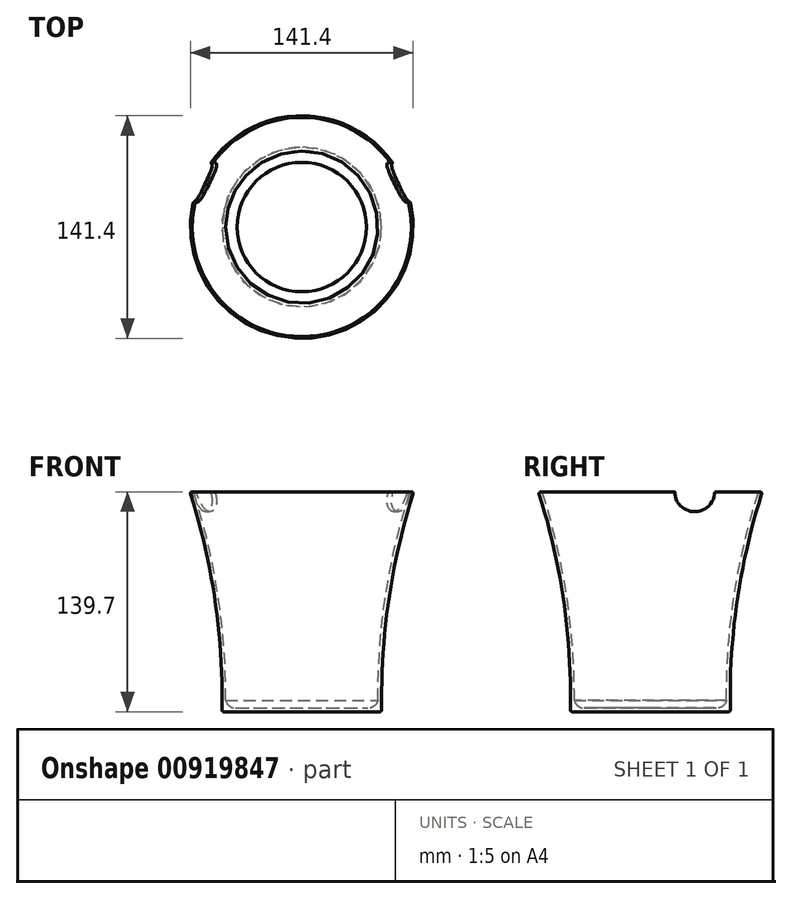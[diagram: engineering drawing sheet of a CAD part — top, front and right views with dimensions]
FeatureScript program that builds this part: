
annotation { "Feature Type Name" : "Feature", "Feature Type Description" : "" }
export const myFeature = defineFeature(function(context is Context, id is Id, definition is map)
    precondition{}
    {
        {
            var Q0;
            Q0=qCreatedBy(makeId("Front.planeOp"),FACE);
            var sketch = newSketch(context, id + "F0", { "sketchPlane" : qUnion([Q0])});
            skLineSegment(sketch, "E0", {"start": v(0, -79.42) * mm, "end": v(50.8, -79.42) * mm});
            skArc(sketch, "E1", {"start": v(76.2, 75.16) * mm, "mid": v(56.34, -0.95) * mm, "end": v(50.8, -79.42) * mm});
            skLineSegment(sketch, "E2", {"start": v(76.2, 75.16) * mm, "end": v(73.82, 75.16) * mm});
            skArc(sketch, "E3", {"start": v(73.82, 75.16) * mm, "mid": v(54.6, 2.68) * mm, "end": v(48.37, -72.04) * mm});
            skLineSegment(sketch, "E4", {"start": v(0, -79.42) * mm, "end": v(0, -77.03) * mm});
            skLineSegment(sketch, "E5", {"start": v(0, -77.03) * mm, "end": v(41.11, -77.03) * mm});
            skArc(sketch, "E6", {"start": v(41.11, -77.03) * mm, "mid": v(45.72, -75.96) * mm, "end": v(48.37, -72.04) * mm});
            skPoint(sketch, "E7", {"position": v(0, -5.65) * mm});
            skLineSegment(sketch, "E8", {"start": v(0, -79.42) * mm, "end": v(0, 60.28) * mm, "construction": true});
            skLineSegment(sketch, "E9", {"start": v(0, 60.28) * mm, "end": v(71.12, 60.28) * mm});
            skSolve(sketch);
        }
        {
            var Q0;
            Q0=makeQuery(id+"F0.imprint","IMPRINT",FACE,{"disambiguationData":[TD([[makeQuery(id+"F0.imprint","IMPRINT",EDGE,{"derivedFrom":sQuery(id+"F0.wireOp",EDGE,"E0")}),1.0]])]});
            var sketch = newSketch(context, id + "F1", { "sketchPlane" : qUnion([Q0])});
            skPoint(sketch, "E10.start.orphan", {"position": v(0, -76.16) * mm});
            skSolve(sketch);
        }
        {
            var Q0;
            Q0=makeQuery(id+"F1.imprint","IMPRINT",FACE,{"disambiguationData":[TD([[makeQuery(id+"F1.imprint","IMPRINT",EDGE,{"derivedFrom":makeQuery(id+"F0.imprint","IMPRINT",EDGE,{"derivedFrom":sQuery(id+"F0.wireOp",EDGE,"E0")})}),1.0]])]});
            var Q1;
            Q1=sQuery(id+"F0.wireOp",EDGE,"E4");
            revolve(context, id + "F2", {"surfaceOperationType" : NewSurfaceOperationType.NEW, "entities" : qUnion([Q0]), "axis" : qUnion([Q1]), "revolveType" : RevolveType.FULL});
        }
        {
            var Q0;
            Q0=qCreatedBy(makeId("Right.planeOp"),FACE);
            var sketch = newSketch(context, id + "F3", { "sketchPlane" : qUnion([Q0])});
            skLineSegment(sketch, "E11", {"start": v(28.17, 63.54) * mm, "end": v(40.87, 63.54) * mm});
            skLineSegment(sketch, "E12", {"start": v(28.17, 63.54) * mm, "end": v(15.47, 63.54) * mm});
            skLineSegment(sketch, "E13", {"start": v(15.47, 63.54) * mm, "end": v(15.47, 60.36) * mm});
            skLineSegment(sketch, "E14", {"start": v(40.87, 63.54) * mm, "end": v(40.87, 60.36) * mm});
            skPoint(sketch, "E15", {"position": v(84.53, 63.54) * mm});
            skArc(sketch, "E16", {"start": v(15.47, 60.36) * mm, "mid": v(28.17, 47.66) * mm, "end": v(40.87, 60.36) * mm});
            skSolve(sketch);
        }
        {
            var Q0;
            Q0=makeQuery(id+"F3.imprint","IMPRINT",FACE,{"disambiguationData":[TD([[makeQuery(id+"F3.imprint","IMPRINT",EDGE,{"derivedFrom":sQuery(id+"F3.wireOp",EDGE,"E11")}),-1.0]])]});
            extrude(context, id + "F4", {"entities" : qUnion([Q0]), "operationType" : NewBodyOperationType.REMOVE, "endBound" : BoundingType.SYMMETRIC, "depth" : 177.8 * mm, "offsetDistance" : 25.4 * mm});
        }
        {
            var Q0;
            Q0=makeQuery(id+"F2.opRevolve","SWEPT_EDGE",EDGE,{"disambiguationData":[OSD([sQuery(id+"F0.wireOp",EDGE,"E0"),sQuery(id+"F0.wireOp",EDGE,"E1")])]});
            fillet(context, id + "F5", {"entities" : qUnion([Q0]), "radius" : 1.27 * mm, "tangentPropagation" : true, "allowEdgeOverflow" : false});
        }
        {
            var Q0;
            {var subQ0=sQuery(id+"F1.wireOp",EDGE,"ap5BJ3xG-dSlw-eity-C2BJ-NnthXKLn69fI");var subQ1=sQuery(id+"F0.wireOp",EDGE,"E1");Q0=makeQuery(id+"F4.boolean.opBoolean","SPLIT",EDGE,{"disambiguationData":[TD([makeQuery(id+"F4.opExtrude","SWEPT_FACE",FACE,{"disambiguationData":[OSD([sQuery(id+"F3.wireOp",EDGE,"E14")])]})])],"derivedFrom":makeQuery(id+"F2.opRevolve","SWEPT_EDGE",EDGE,{"disambiguationData":[OSD([subQ1,subQ0])]})});}
            var Q1;
            {var subQ0=sQuery(id+"F1.wireOp",EDGE,"ap5BJ3xG-dSlw-eity-C2BJ-NnthXKLn69fI");var subQ1=sQuery(id+"F0.wireOp",EDGE,"E3");Q1=makeQuery(id+"F4.boolean.opBoolean","SPLIT",EDGE,{"disambiguationData":[TD([makeQuery(id+"F4.opExtrude","SWEPT_FACE",FACE,{"disambiguationData":[OSD([sQuery(id+"F3.wireOp",EDGE,"E14")])]})])],"derivedFrom":makeQuery(id+"F2.opRevolve","SWEPT_EDGE",EDGE,{"disambiguationData":[OSD([subQ1,subQ0])]})});}
            fillet(context, id + "F6", {"entities" : qUnion([Q0, Q1]), "radius" : 1.14 * mm, "tangentPropagation" : true, "allowEdgeOverflow" : false});
        }
    });
